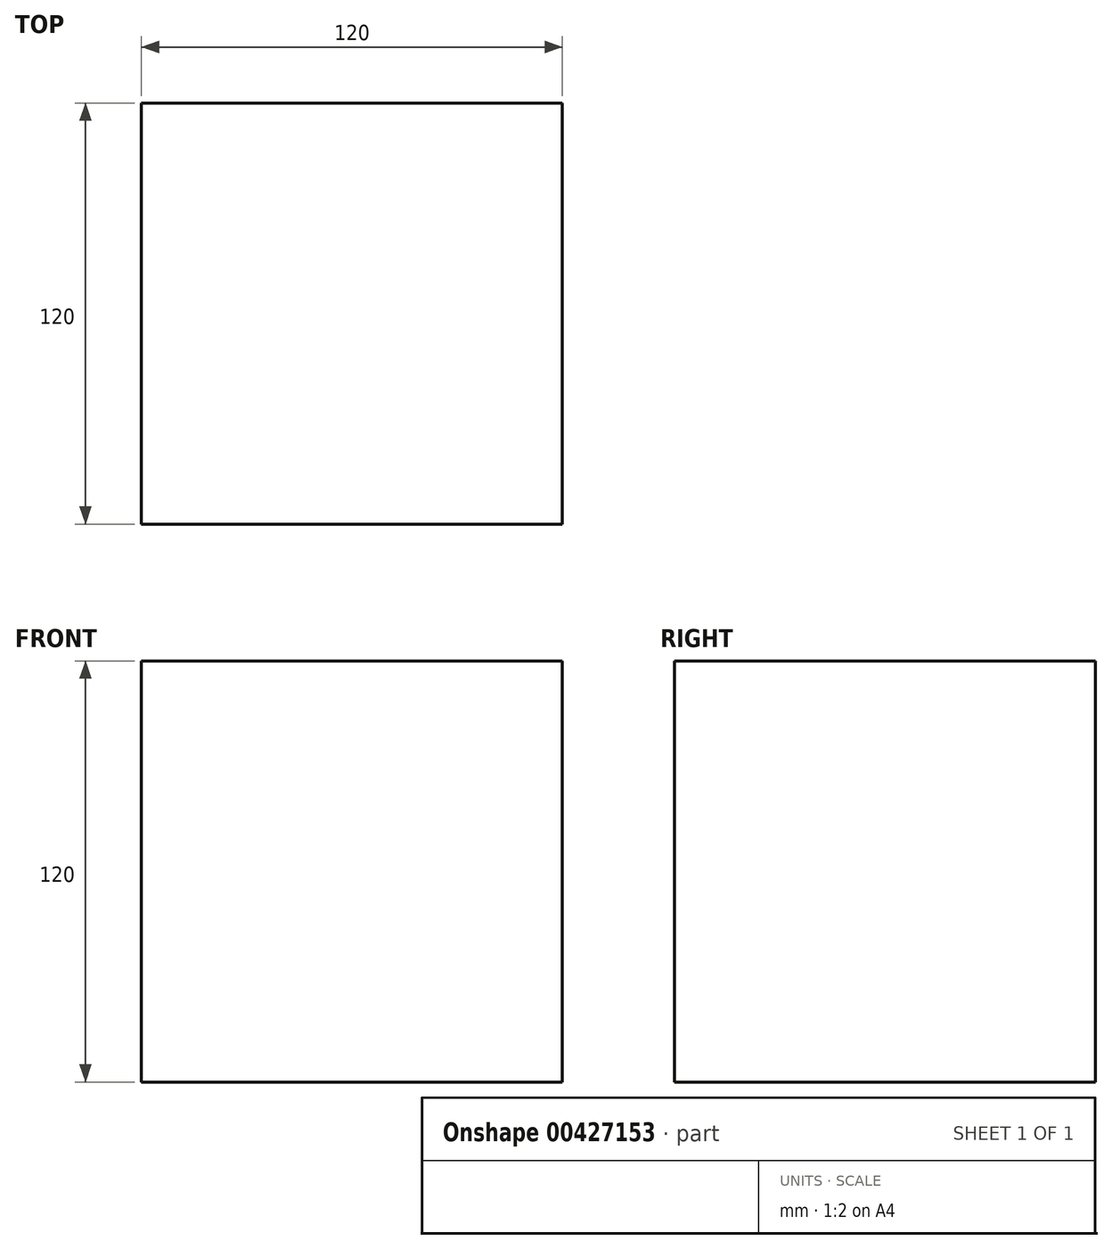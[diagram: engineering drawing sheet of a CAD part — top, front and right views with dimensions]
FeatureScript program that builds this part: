
annotation { "Feature Type Name" : "Feature", "Feature Type Description" : "" }
export const myFeature = defineFeature(function(context is Context, id is Id, definition is map)
    precondition{}
    {
        {
            var Q0;
            Q0=qCreatedBy(makeId("Front.planeOp"),FACE);
            var sketch = newSketch(context, id + "F0", { "sketchPlane" : qUnion([Q0])});
            skLineSegment(sketch, "E0.bottom", {"start": v(60, -60) * mm, "end": v(-60, -60) * mm});
            skLineSegment(sketch, "E0.top", {"start": v(60, 60) * mm, "end": v(-60, 60) * mm});
            skLineSegment(sketch, "E0.left", {"start": v(60, -60) * mm, "end": v(60, 60) * mm});
            skLineSegment(sketch, "E0.right", {"start": v(-60, -60) * mm, "end": v(-60, 60) * mm});
            skPoint(sketch, "E0.middle", {"position": v(0, 0) * mm});
            skSolve(sketch);
        }
        {
            var Q0;
            Q0 = qSketchRegion(id + "F0", true);
            var Q1;
            Q1=makeQuery(id+"F0.imprint","IMPRINT",FACE,{"disambiguationData":[TD([[makeQuery(id+"F0.imprint","IMPRINT",EDGE,{"derivedFrom":sQuery(id+"F0.wireOp",EDGE,"E0.bottom")}),-1.0]])]});
            extrude(context, id + "F1", {"entities" : qUnion([Q0, Q1]), "endBound" : BoundingType.SYMMETRIC, "depth" : 120 * mm});
        }
    });
